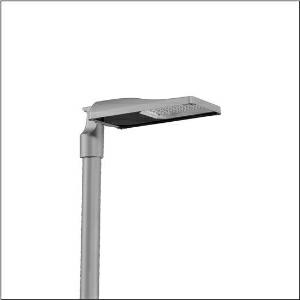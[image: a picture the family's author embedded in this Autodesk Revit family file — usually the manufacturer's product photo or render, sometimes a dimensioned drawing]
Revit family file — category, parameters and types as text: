
# Revit family: streetlight_sl_31_mini___stw1_0a_5xh2e7aa08ja_756d
name_source: partatom
category: Lighting Fixtures
units: mm (PartAtom-declared; Revit-internal decimal feet)

## family parameters
Cut with Voids When Loaded = No
Host = Face
Light Source = No
Part Type = Normal
Room Calculation Point = No
Round Connector Dimension = Use Diameter
Shared = No

## types (1)
- --- (1 x LED, 9800 lm, 81.1 W, 2200K)
    Apparent Load = 81 VA
    CIE Flux Codes = 39 75 98 100 100
    Color Rendering = 70
    Color Temperature = 2200K
    Default Elevation = 1800 mm
    Description = Streetlight SL 31 mini Easy mast luminaire for post-top, side-entry; light control with lens of PMMA; light distribution: STW1.0a, direct asymmetric distribution, for standard-compliant lighting for roads and squares; LED: luminous flux: 9.800lm, light colour: 722, colour temperature: 2200K; luminous efficacy: 120,8lm/W; control: overheat protection, intelligent temperature release in ECG and LED module, constant luminous flux control, time-dependent luminous flux control, flexible luminous flux parameterisation, pre-setting: linear dimming characteristic; luminaire housing, of diecast aluminium, Siteco® metallic grey (DB 702S), corrosivity category C5 high according to DIN EN ISO 12944; cover of toughened safety glass, transparent, mast flange of diecast aluminium, Siteco® metallic grey (DB 702S), spigot size: 76/60mm, mast flange included unmounted; with cable H07RN-F 2x 1.5mm², cable length: 10,5m, connection cable pre-assembled; mains connection: 220..240V, AC, 50/60Hz; power consumption (at start of service life): 81,1W / (at end of service life): 88,3W / (with reduced operation 50%): 36,1W; protection rating (complete): IP66; insulation class (complete): insulation class II (safety insulation); impact resistance: IK10; certification: CE, ENEC, ENEC+, VDE, UKCA; permissible operating ambient temperature for outdoor applications: -40..+50°C; packaging unit: 1 piece

Light Distribution: STW1.0a
    Height = 76 mm
    Lamp = 1 x LED
    Lamp Light Flux = 9800 lm
    Lamp Power = 81.1 W
    Lamp count = 1
    Length = 547 mm
    Luminous efficacy = 121 lm/W
    Manufacturer = Siteco
    ModVariant = No
    Model = 5XH2E7AA08JA
    Number of Poles = 1
    OnlyDefault = Yes
    Power Factor = 1
    Product Name = Streetlight SL 31 mini | STW1.0a
    Product group = mast luminaire | pylon top
    ProductGroupID = 6100
    Protection Class = Protection class II
    Protection Degree = IP 66
    RLX_Detail_Level = 1
    RLX_Emergency_Light_Flux = 0 lm
    RLX_Emergency_Type = 0
    RLX_Emergency_Type_DB = No
    RlxData = <blob elided: 39633 chars, md5=5199f98f>
    Socket = socket
    Standby Power = 0 W
    System Light Flux = 9800 lm
    System Power = 81 W
    Type Comments = factory setting: luminous flux: 100 % | dim-lin: 254 | 860 mA
    Type Image = l_1300326.jpg
    URL = http://relux.com
    VarID = @adj_008429
    Voltage = 0 V
    Weight = 0.00 kg
    Width = 265 mm

## geometry (parser evidence)
native form markers: Blend x4, Sweep x10
no freeform markers — native parametric forms only
